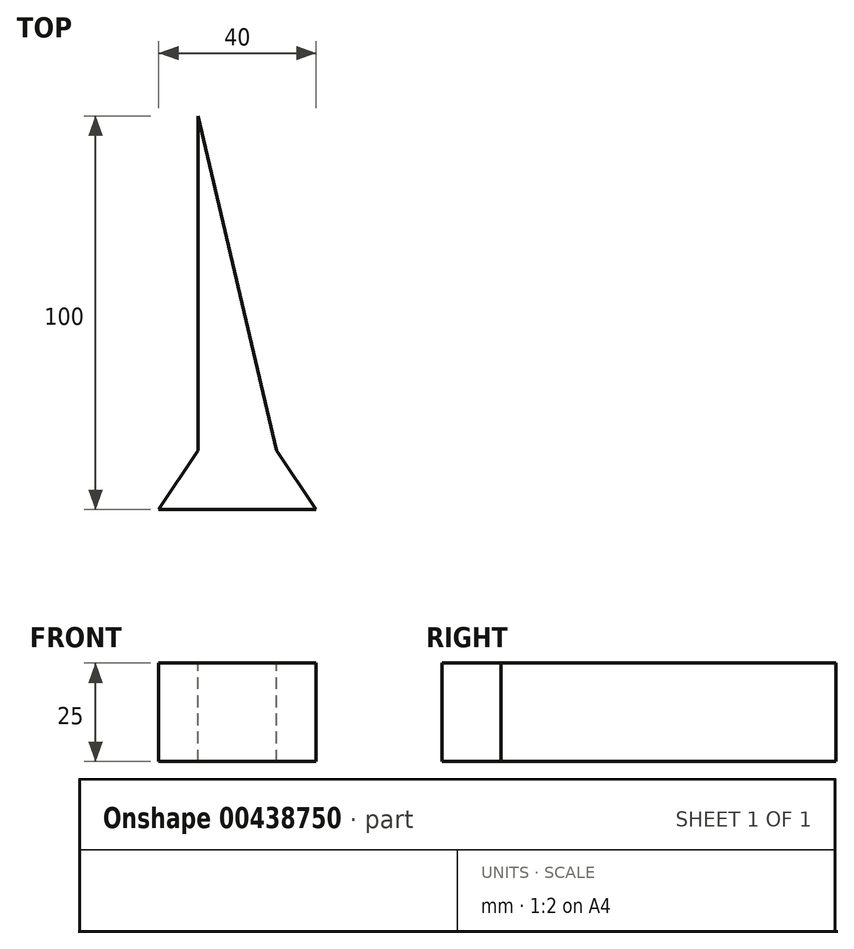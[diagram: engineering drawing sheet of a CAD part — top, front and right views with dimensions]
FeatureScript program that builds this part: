
annotation { "Feature Type Name" : "Feature", "Feature Type Description" : "" }
export const myFeature = defineFeature(function(context is Context, id is Id, definition is map)
    precondition{}
    {
        {
            var Q0;
            Q0=qCreatedBy(makeId("Top.planeOp"),FACE);
            var sketch = newSketch(context, id + "F0", { "sketchPlane" : qUnion([Q0])});
            skLineSegment(sketch, "E0.bottom", {"start": v(-6.62, -32.62) * mm, "end": v(13.38, -32.62) * mm});
            skLineSegment(sketch, "E0.top", {"start": v(-6.62, -47.62) * mm, "end": v(13.38, -47.62) * mm});
            skLineSegment(sketch, "E0.left", {"start": v(-6.62, -32.62) * mm, "end": v(-6.62, -47.62) * mm});
            skLineSegment(sketch, "E0.right", {"start": v(13.38, -32.62) * mm, "end": v(13.38, -47.62) * mm});
            skLineSegment(sketch, "E1", {"start": v(-16.62, -47.62) * mm, "end": v(-6.62, -32.62) * mm});
            skLineSegment(sketch, "E2", {"start": v(-16.62, -47.62) * mm, "end": v(-6.62, -47.62) * mm});
            skLineSegment(sketch, "E3", {"start": v(23.38, -47.62) * mm, "end": v(13.38, -32.62) * mm});
            skLineSegment(sketch, "E4", {"start": v(23.38, -47.62) * mm, "end": v(13.38, -47.62) * mm});
            skLineSegment(sketch, "E5", {"start": v(-6.62, 52.38) * mm, "end": v(-6.62, -32.62) * mm});
            skLineSegment(sketch, "E6", {"start": v(-6.62, 52.38) * mm, "end": v(13.38, -32.62) * mm});
            skSolve(sketch);
        }
        {
            var Q0;
            Q0=makeQuery(id+"F0.imprint","IMPRINT",FACE,{"disambiguationData":[TD([[makeQuery(id+"F0.imprint","IMPRINT",EDGE,{"derivedFrom":sQuery(id+"F0.wireOp",EDGE,"E0.bottom")}),1.0]])]});
            var Q1;
            Q1=makeQuery(id+"F0.imprint","IMPRINT",FACE,{"disambiguationData":[TD([[makeQuery(id+"F0.imprint","IMPRINT",EDGE,{"derivedFrom":sQuery(id+"F0.wireOp",EDGE,"E0.bottom")}),-1.0]])]});
            var Q2;
            Q2=makeQuery(id+"F0.imprint","IMPRINT",FACE,{"disambiguationData":[TD([[makeQuery(id+"F0.imprint","IMPRINT",EDGE,{"derivedFrom":sQuery(id+"F0.wireOp",EDGE,"E0.left")}),-1.0]])]});
            var Q3;
            Q3=makeQuery(id+"F0.imprint","IMPRINT",FACE,{"disambiguationData":[TD([[makeQuery(id+"F0.imprint","IMPRINT",EDGE,{"derivedFrom":sQuery(id+"F0.wireOp",EDGE,"E0.right")}),1.0]])]});
            extrude(context, id + "F1", {"entities" : qUnion([Q0, Q1, Q2, Q3]), "oppositeDirection" : true, "depth" : 25 * mm});
        }
    });
